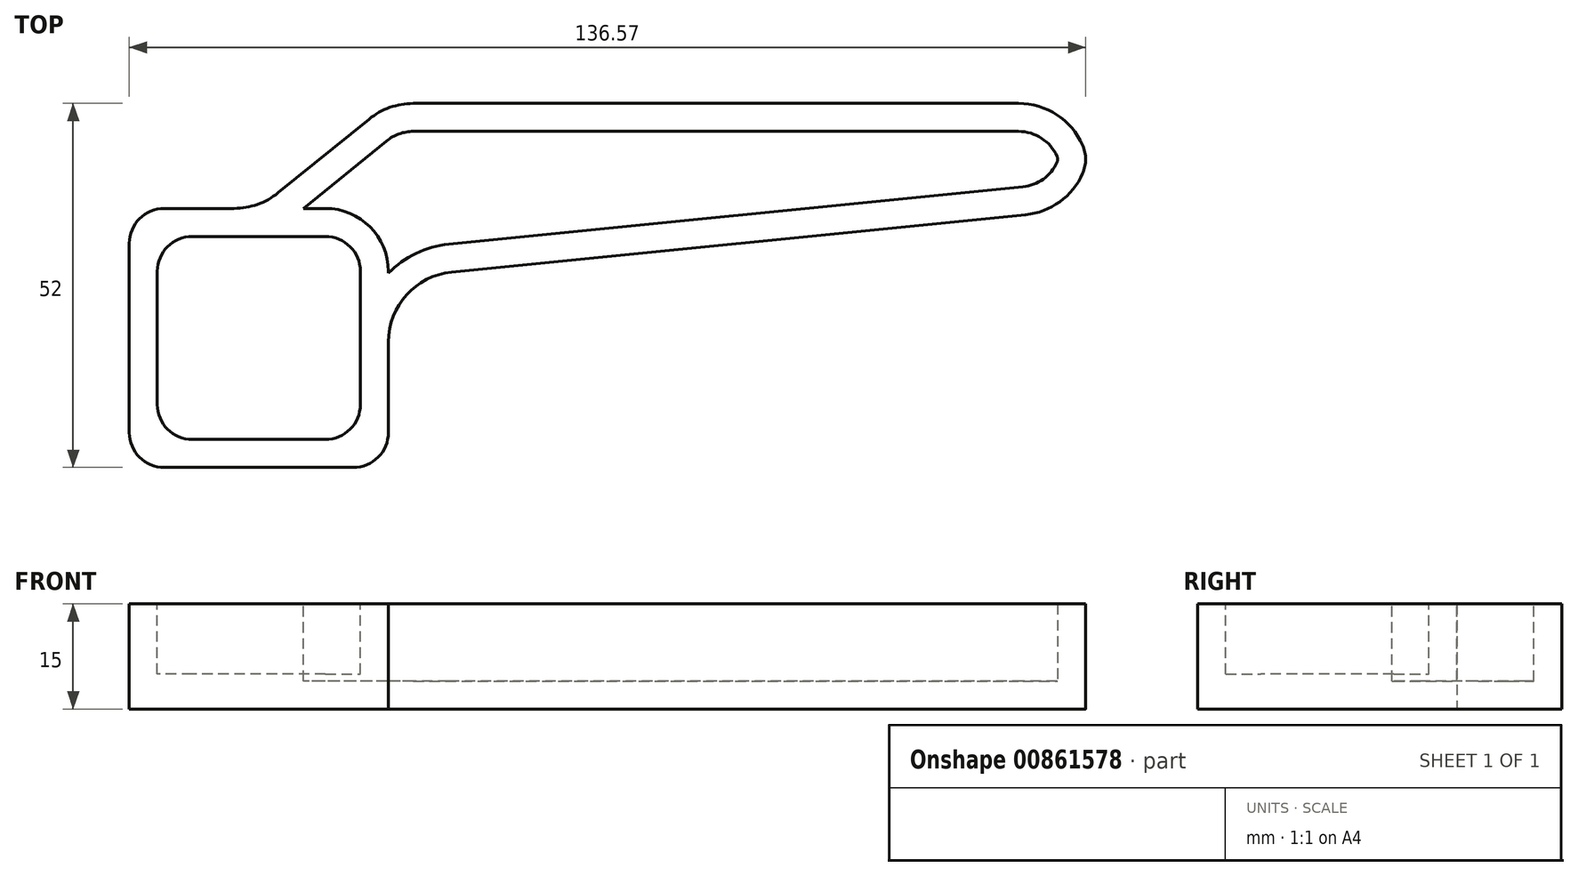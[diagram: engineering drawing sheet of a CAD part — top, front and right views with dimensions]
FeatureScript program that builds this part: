
annotation { "Feature Type Name" : "Feature", "Feature Type Description" : "" }
export const myFeature = defineFeature(function(context is Context, id is Id, definition is map)
    precondition{}
    {
        {
            var Q0;
            Q0=qCreatedBy(makeId("Top.planeOp"),FACE);
            var sketch = newSketch(context, id + "F0", { "sketchPlane" : qUnion([Q0])});
            skLineSegment(sketch, "E0.bottom", {"start": v(18.5, 18.5) * mm, "end": v(-18.5, 18.5) * mm});
            skLineSegment(sketch, "E0.top", {"start": v(18.5, -18.5) * mm, "end": v(-18.5, -18.5) * mm});
            skLineSegment(sketch, "E0.left", {"start": v(18.5, 18.5) * mm, "end": v(18.5, -18.5) * mm});
            skLineSegment(sketch, "E0.right", {"start": v(-18.5, 18.5) * mm, "end": v(-18.5, -18.5) * mm});
            skPoint(sketch, "E0.middle", {"position": v(0, 0) * mm});
            skLineSegment(sketch, "E1.bottom", {"start": v(18.5, 18.5) * mm, "end": v(118.5, 18.5) * mm});
            skLineSegment(sketch, "E1.top", {"start": v(18.5, 33.5) * mm, "end": v(118.5, 33.5) * mm});
            skLineSegment(sketch, "E1.left", {"start": v(18.5, 18.5) * mm, "end": v(18.5, 33.5) * mm});
            skLineSegment(sketch, "E1.right", {"start": v(118.5, 18.5) * mm, "end": v(118.5, 33.5) * mm});
            skLineSegment(sketch, "E2", {"start": v(118.5, 18.5) * mm, "end": v(18.5, 8.5) * mm});
            skLineSegment(sketch, "E3", {"start": v(18.5, 33.5) * mm, "end": v(0, 18.5) * mm});
            skSolve(sketch);
        }
        {
            var Q0;
            Q0 = qSketchRegion(id + "F0", true);
            extrude(context, id + "F1", {"entities" : qUnion([Q0]), "depth" : 15 * mm, "offsetDistance" : 25 * mm});
        }
        {
            var Q0;
            Q0=makeQuery(id+"F1.opExtrude","CAP_FACE",FACE,{"disambiguationData":[OSD([sQuery(id+"F0.wireOp",EDGE,"E0.bottom"),sQuery(id+"F0.wireOp",EDGE,"E0.top"),sQuery(id+"F0.wireOp",EDGE,"E0.left"),sQuery(id+"F0.wireOp",EDGE,"E0.right"),sQuery(id+"F0.wireOp",EDGE,"E1.top"),sQuery(id+"F0.wireOp",EDGE,"E1.right"),sQuery(id+"F0.wireOp",EDGE,"E2"),sQuery(id+"F0.wireOp",EDGE,"E3")])],"isStart":false});
            var sketch = newSketch(context, id + "F2", { "sketchPlane" : qUnion([Q0])});
            skLineSegment(sketch, "E4.bottom", {"start": v(14.5, 14.5) * mm, "end": v(-14.5, 14.5) * mm});
            skLineSegment(sketch, "E4.top", {"start": v(14.5, -14.5) * mm, "end": v(-14.5, -14.5) * mm});
            skLineSegment(sketch, "E4.left", {"start": v(14.5, 14.5) * mm, "end": v(14.5, -14.5) * mm});
            skLineSegment(sketch, "E4.right", {"start": v(-14.5, 14.5) * mm, "end": v(-14.5, -14.5) * mm});
            skPoint(sketch, "E4.middle", {"position": v(0, 0) * mm});
            skSolve(sketch);
        }
        {
            var Q0;
            Q0 = qSketchRegion(id + "F2", true);
            extrude(context, id + "F3", {"entities" : qUnion([Q0]), "operationType" : NewBodyOperationType.REMOVE, "oppositeDirection" : true, "depth" : 10 * mm, "offsetDistance" : 25 * mm});
        }
        {
            var Q0;
            Q0=makeQuery(id+"F1.opExtrude","SWEPT_EDGE",EDGE,{"disambiguationData":[OSD([sQuery(id+"F0.wireOp",EDGE,"E0.bottom"),sQuery(id+"F0.wireOp",EDGE,"E3")])]});
            var Q1;
            Q1=makeQuery(id+"F1.opExtrude","SWEPT_EDGE",EDGE,{"disambiguationData":[OSD([sQuery(id+"F0.wireOp",EDGE,"E1.top"),sQuery(id+"F0.wireOp",EDGE,"E1.left"),sQuery(id+"F0.wireOp",EDGE,"E3")])]});
            var Q2;
            Q2=makeQuery(id+"F1.opExtrude","SWEPT_EDGE",EDGE,{"disambiguationData":[OSD([sQuery(id+"F0.wireOp",EDGE,"E0.left"),sQuery(id+"F0.wireOp",EDGE,"E2")])]});
            var Q3;
            Q3=makeQuery(id+"F1.opExtrude","SWEPT_EDGE",EDGE,{"disambiguationData":[OSD([sQuery(id+"F0.wireOp",EDGE,"E1.bottom"),sQuery(id+"F0.wireOp",EDGE,"E1.right"),sQuery(id+"F0.wireOp",EDGE,"E2")])]});
            var Q4;
            Q4=makeQuery(id+"F1.opExtrude","SWEPT_EDGE",EDGE,{"disambiguationData":[OSD([sQuery(id+"F0.wireOp",EDGE,"E1.top"),sQuery(id+"F0.wireOp",EDGE,"E1.right")])]});
            fillet(context, id + "F4", {"entities" : qUnion([Q0, Q1, Q2, Q3, Q4]), "radius" : 10 * mm, "tangentPropagation" : true, "allowEdgeOverflow" : false});
        }
        {
            var Q0;
            Q0=makeQuery(id+"F1.opExtrude","SWEPT_EDGE",EDGE,{"disambiguationData":[OSD([sQuery(id+"F0.wireOp",EDGE,"E0.bottom"),sQuery(id+"F0.wireOp",EDGE,"E0.right")])]});
            var Q1;
            Q1=makeQuery(id+"F3.boolean.opBoolean","COPY",EDGE,{"derivedFrom":makeQuery(id+"F3.opExtrude","SWEPT_EDGE",EDGE,{"disambiguationData":[OSD([sQuery(id+"F2.wireOp",EDGE,"E4.bottom"),sQuery(id+"F2.wireOp",EDGE,"E4.right")])]})});
            var Q2;
            Q2=makeQuery(id+"F3.boolean.opBoolean","COPY",EDGE,{"derivedFrom":makeQuery(id+"F3.opExtrude","SWEPT_EDGE",EDGE,{"disambiguationData":[OSD([sQuery(id+"F2.wireOp",EDGE,"E4.bottom"),sQuery(id+"F2.wireOp",EDGE,"E4.left")])]})});
            var Q3;
            Q3=makeQuery(id+"F1.opExtrude","SWEPT_EDGE",EDGE,{"disambiguationData":[OSD([sQuery(id+"F0.wireOp",EDGE,"E0.top"),sQuery(id+"F0.wireOp",EDGE,"E0.right")])]});
            var Q4;
            Q4=makeQuery(id+"F1.opExtrude","SWEPT_EDGE",EDGE,{"disambiguationData":[OSD([sQuery(id+"F0.wireOp",EDGE,"E0.top"),sQuery(id+"F0.wireOp",EDGE,"E0.left")])]});
            var Q5;
            Q5=makeQuery(id+"F3.boolean.opBoolean","COPY",EDGE,{"derivedFrom":makeQuery(id+"F3.opExtrude","SWEPT_EDGE",EDGE,{"disambiguationData":[OSD([sQuery(id+"F2.wireOp",EDGE,"E4.top"),sQuery(id+"F2.wireOp",EDGE,"E4.right")])]})});
            var Q6;
            Q6=makeQuery(id+"F3.boolean.opBoolean","COPY",EDGE,{"derivedFrom":makeQuery(id+"F3.opExtrude","SWEPT_EDGE",EDGE,{"disambiguationData":[OSD([sQuery(id+"F2.wireOp",EDGE,"E4.top"),sQuery(id+"F2.wireOp",EDGE,"E4.left")])]})});
            var Q7;
            {var subQ0=sQuery(id+"F0.wireOp",EDGE,"E1.right");Q7=makeQuery(id+"F4.opFillet","BLEND_EDGE",EDGE,{"blendedFrom":[makeQuery(id+"F1.opExtrude","SWEPT_EDGE",EDGE,{"disambiguationData":[OSD([sQuery(id+"F0.wireOp",EDGE,"E1.bottom"),subQ0,sQuery(id+"F0.wireOp",EDGE,"E2")])]}),makeQuery(id+"F1.opExtrude","SWEPT_EDGE",EDGE,{"disambiguationData":[OSD([sQuery(id+"F0.wireOp",EDGE,"E1.top"),subQ0])]})],"blendedInto":[]});}
            fillet(context, id + "F5", {"entities" : qUnion([Q0, Q1, Q2, Q3, Q4, Q5, Q6, Q7]), "radius" : 5 * mm, "tangentPropagation" : true, "allowEdgeOverflow" : false});
        }
        {
            var Q0;
            Q0=makeQuery(id+"F1.opExtrude","CAP_FACE",FACE,{"disambiguationData":[OSD([sQuery(id+"F0.wireOp",EDGE,"E0.bottom"),sQuery(id+"F0.wireOp",EDGE,"E0.top"),sQuery(id+"F0.wireOp",EDGE,"E0.left"),sQuery(id+"F0.wireOp",EDGE,"E0.right"),sQuery(id+"F0.wireOp",EDGE,"E1.top"),sQuery(id+"F0.wireOp",EDGE,"E1.right"),sQuery(id+"F0.wireOp",EDGE,"E2"),sQuery(id+"F0.wireOp",EDGE,"E3")])],"isStart":false});
            shell(context, id + "F6", {"entities" : qUnion([Q0]), "thickness" : 4 * mm});
        }
    });
